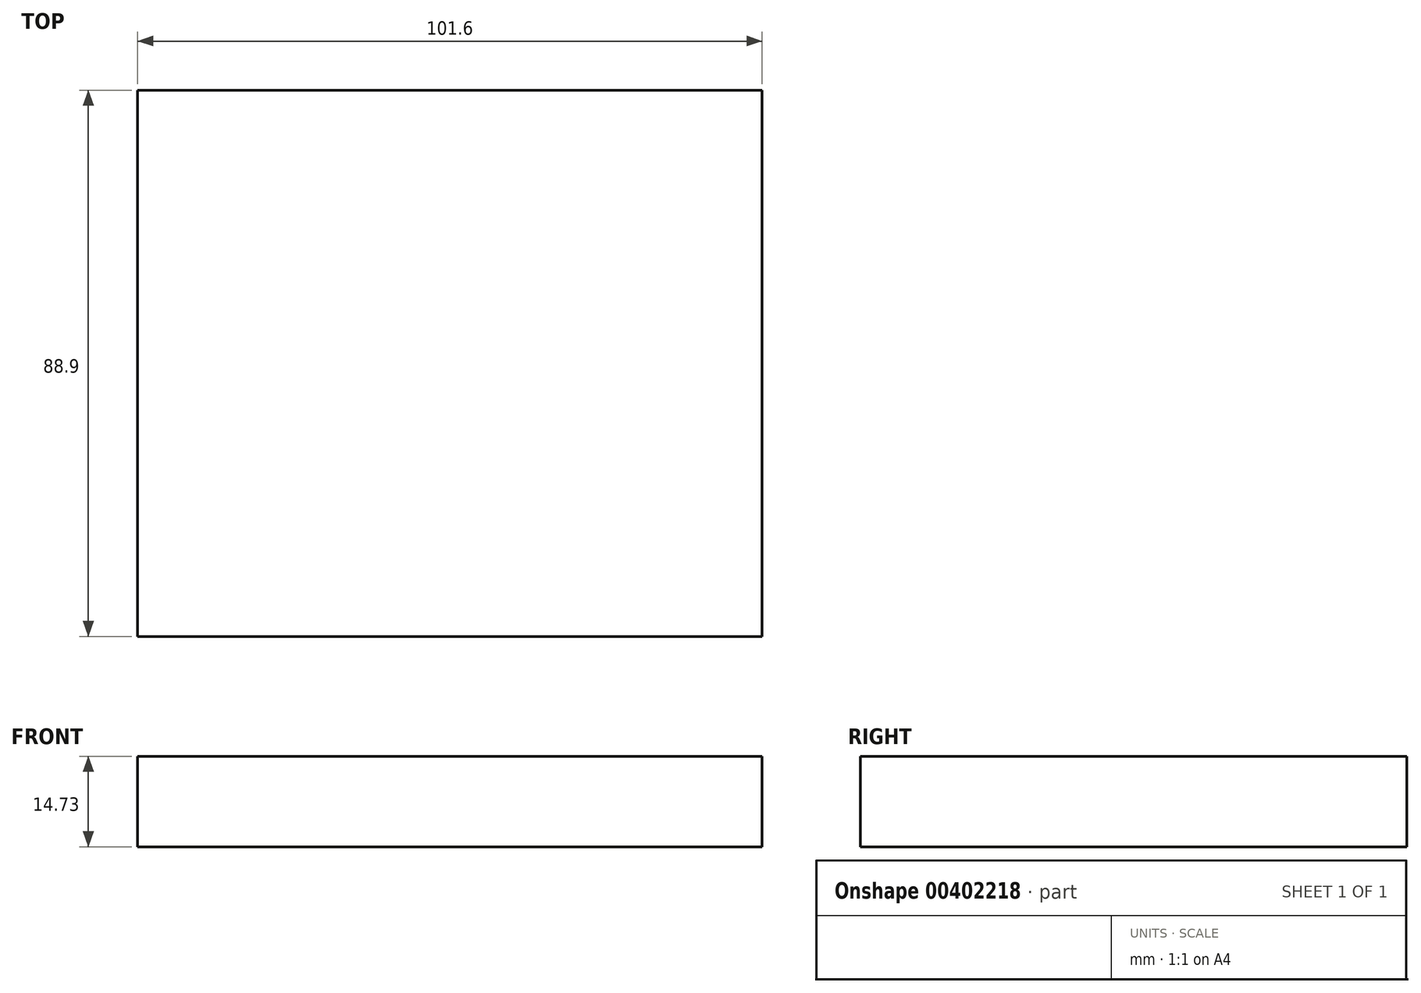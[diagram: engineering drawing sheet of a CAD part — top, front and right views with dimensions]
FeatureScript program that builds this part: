
annotation { "Feature Type Name" : "Feature", "Feature Type Description" : "" }
export const myFeature = defineFeature(function(context is Context, id is Id, definition is map)
    precondition{}
    {
        {
            var Q0;
            Q0=qCreatedBy(makeId("Top.planeOp"),FACE);
            var sketch = newSketch(context, id + "F0", { "sketchPlane" : qUnion([Q0])});
            skLineSegment(sketch, "E0.bottom", {"start": v(0, 0) * mm, "end": v(101.6, 0) * mm});
            skLineSegment(sketch, "E0.top", {"start": v(0, 88.9) * mm, "end": v(101.6, 88.9) * mm});
            skLineSegment(sketch, "E0.left", {"start": v(0, 0) * mm, "end": v(0, 88.9) * mm});
            skLineSegment(sketch, "E0.right", {"start": v(101.6, 0) * mm, "end": v(101.6, 88.9) * mm});
            skSolve(sketch);
        }
        {
            var Q0;
            Q0 = qSketchRegion(id + "F0", true);
            extrude(context, id + "F1", {"entities" : qUnion([Q0]), "depth" : 14.73 * mm});
        }
    });
